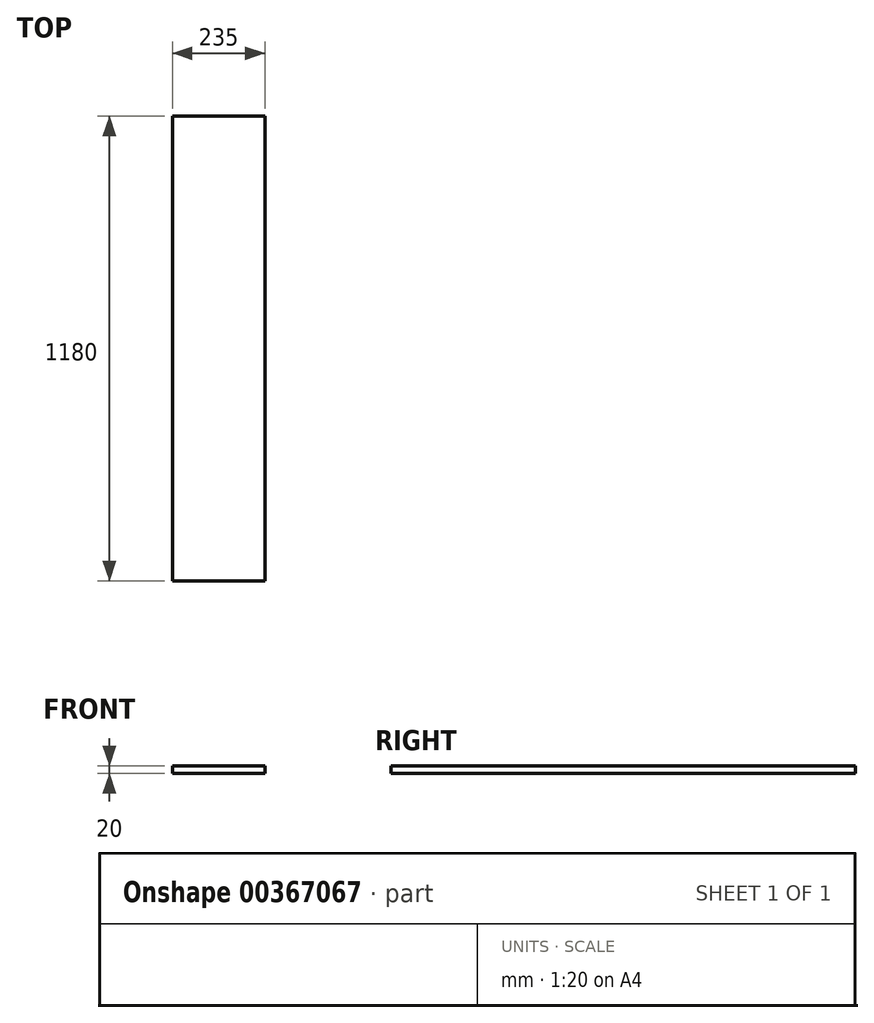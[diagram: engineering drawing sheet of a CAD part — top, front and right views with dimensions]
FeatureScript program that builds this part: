
annotation { "Feature Type Name" : "Feature", "Feature Type Description" : "" }
export const myFeature = defineFeature(function(context is Context, id is Id, definition is map)
    precondition{}
    {
        {
            var Q0;
            Q0=qCreatedBy(makeId("Top.planeOp"),FACE);
            var sketch = newSketch(context, id + "F0", { "sketchPlane" : qUnion([Q0])});
            skLineSegment(sketch, "E0.bottom", {"start": v(117.5, -590) * mm, "end": v(-117.5, -590) * mm});
            skLineSegment(sketch, "E0.top", {"start": v(117.5, 590) * mm, "end": v(-117.5, 590) * mm});
            skLineSegment(sketch, "E0.left", {"start": v(117.5, -590) * mm, "end": v(117.5, 590) * mm});
            skLineSegment(sketch, "E0.right", {"start": v(-117.5, -590) * mm, "end": v(-117.5, 590) * mm});
            skPoint(sketch, "E0.middle", {"position": v(0, 0) * mm});
            skSolve(sketch);
        }
        {
            var Q0;
            Q0 = qSketchRegion(id + "F0", true);
            extrude(context, id + "F1", {"entities" : qUnion([Q0]), "depth" : 20 * mm});
        }
    });
